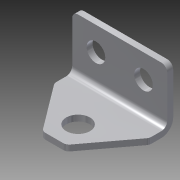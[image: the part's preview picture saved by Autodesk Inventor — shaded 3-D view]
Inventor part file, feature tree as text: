
AUTODESK INVENTOR PART (.ipt)
format: ipt  version: 2014 (Build 180170000, 170)  size: 157,184 bytes
history: native  units: in
note: dims shown in document units (in); Inventor stores cm internally (conversion verified against a paired STEP export)
features: sheet_metal_op x4, sketch x3, other x2, extrude x1, fillet x1
ambient origin geometry x8: Origin, YZ Plane, XZ Plane, XY Plane, X Axis, Y Axis, Z Axis, Center Point
bodies: Solid1 (feature_tree)
feature tree (11):
  sheet_metal_op  "Face1"
  sheet_metal_op  "Flange1"
  extrude  "Extrusion1"  Depth=0.5in
  fillet  "Fillet1"  Radius=0.196in
  sketch  "Sketch1"  dims[d0=1.0in d1=0.5in d2=0.196in]
  other  "Plate1"
  sketch  "Sketch2"  dims[d3=0.196in]
  other  "Plate2"
  sheet_metal_op  "Bend1"
  sheet_metal_op  "Corner1"
  sketch  "Sketch3"  dims[d4=0.25in d5=0.25in d6=0.25in d7=0.25in d8=0.0625in d9=0.0625in d10=0.0312in d11=0.125in d12=0.0625in d13=0.75in d14=90.0deg d15=0.0625in d16=0.25in d17=0.0625in d18=0.0625in d19=0.125in d20=0.125in d21=0.25in d22=0.25in d23=1.0in d24=0.0in d25=0.0625in]
